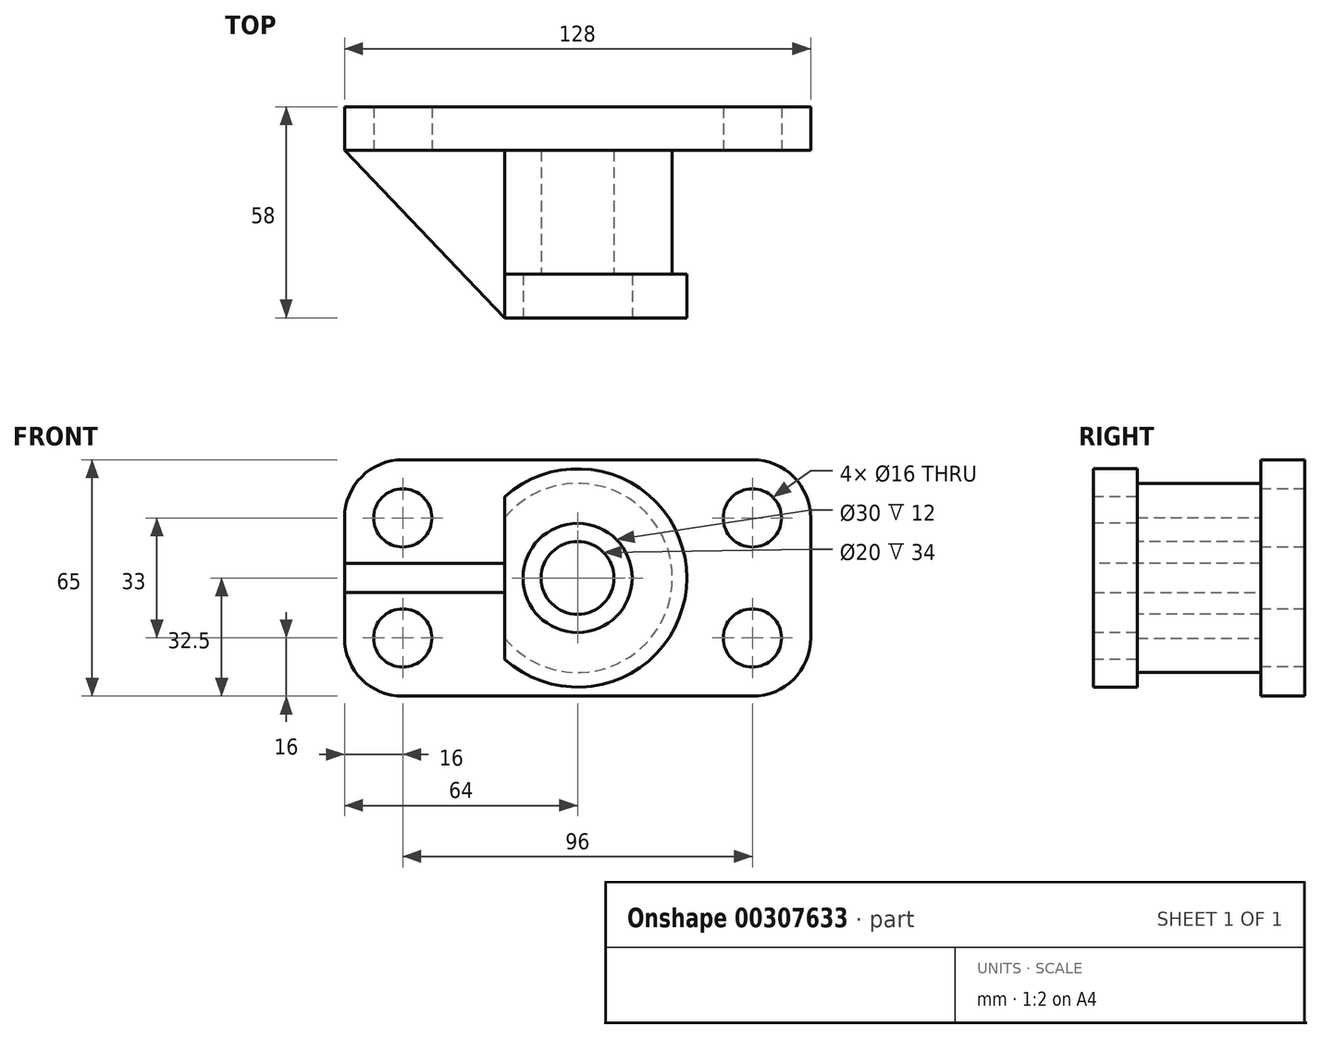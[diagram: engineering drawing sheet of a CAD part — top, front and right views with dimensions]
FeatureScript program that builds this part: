
annotation { "Feature Type Name" : "Feature", "Feature Type Description" : "" }
export const myFeature = defineFeature(function(context is Context, id is Id, definition is map)
    precondition{}
    {
        {
            var Q0;
            Q0=qCreatedBy(makeId("Front.planeOp"),FACE);
            var sketch = newSketch(context, id + "F0", { "sketchPlane" : qUnion([Q0])});
            skLineSegment(sketch, "E0", {"start": v(0, 0) * mm, "end": v(-128, 0) * mm});
            skLineSegment(sketch, "E1", {"start": v(0, 0) * mm, "end": v(0, 65) * mm});
            skLineSegment(sketch, "E2", {"start": v(0, 65) * mm, "end": v(-128, 65) * mm});
            skLineSegment(sketch, "E3", {"start": v(-128, 0) * mm, "end": v(-128, 65) * mm});
            skSolve(sketch);
        }
        {
            var Q0;
            Q0=makeQuery(id+"F0.imprint","IMPRINT",FACE,{"disambiguationData":[TD([[makeQuery(id+"F0.imprint","IMPRINT",EDGE,{"derivedFrom":sQuery(id+"F0.wireOp",EDGE,"E0")}),-1.0]])]});
            extrude(context, id + "F1", {"entities" : qUnion([Q0]), "depth" : 12 * mm});
        }
        {
            var Q0;
            Q0=makeQuery(id+"F1.opExtrude","SWEPT_EDGE",EDGE,{"disambiguationData":[OSD([sQuery(id+"F0.wireOp",EDGE,"E2"),sQuery(id+"F0.wireOp",EDGE,"E3")])]});
            var Q1;
            Q1=makeQuery(id+"F1.opExtrude","SWEPT_EDGE",EDGE,{"disambiguationData":[OSD([sQuery(id+"F0.wireOp",EDGE,"E0"),sQuery(id+"F0.wireOp",EDGE,"E3")])]});
            var Q2;
            Q2=makeQuery(id+"F1.opExtrude","SWEPT_EDGE",EDGE,{"disambiguationData":[OSD([sQuery(id+"F0.wireOp",EDGE,"E1"),sQuery(id+"F0.wireOp",EDGE,"E2")])]});
            var Q3;
            Q3=makeQuery(id+"F1.opExtrude","SWEPT_EDGE",EDGE,{"disambiguationData":[OSD([sQuery(id+"F0.wireOp",EDGE,"E0"),sQuery(id+"F0.wireOp",EDGE,"E1")])]});
            fillet(context, id + "F2", {"entities" : qUnion([Q0, Q1, Q2, Q3]), "radius" : 16 * mm, "tangentPropagation" : true, "allowEdgeOverflow" : false});
        }
        {
            var Q0;
            Q0=makeQuery(id+"F1.opExtrude","CAP_FACE",FACE,{"disambiguationData":[OSD([sQuery(id+"F0.wireOp",EDGE,"E0"),sQuery(id+"F0.wireOp",EDGE,"E1"),sQuery(id+"F0.wireOp",EDGE,"E2"),sQuery(id+"F0.wireOp",EDGE,"E3")])],"isStart":false});
            var sketch = newSketch(context, id + "F3", { "sketchPlane" : qUnion([Q0])});
            skLineSegment(sketch, "E4", {"start": v(-112, 65) * mm, "end": v(-16, 65) * mm});
            skCircle(sketch, "E5", {"center": v(-64, 32.5) * mm, "radius": 26 * mm});
            skSolve(sketch);
        }
        {
            var Q0;
            Q0 = qSketchRegion(id + "F3", true);
            extrude(context, id + "F4", {"entities" : qUnion([Q0]), "operationType" : NewBodyOperationType.ADD, "depth" : 34 * mm});
        }
        {
            var Q0;
            Q0=makeQuery(id+"F4.opExtrude","CAP_FACE",FACE,{"disambiguationData":[OSD([sQuery(id+"F3.wireOp",EDGE,"E5")])],"isStart":false});
            var sketch = newSketch(context, id + "F5", { "sketchPlane" : qUnion([Q0])});
            skCircle(sketch, "E6", {"center": v(-64, 32.5) * mm, "radius": 30 * mm});
            skSolve(sketch);
        }
        {
            var Q0;
            Q0 = qSketchRegion(id + "F5", true);
            extrude(context, id + "F6", {"entities" : qUnion([Q0]), "operationType" : NewBodyOperationType.ADD, "depth" : 12 * mm});
        }
        {
            var Q0;
            Q0=makeQuery(id+"F6.opExtrude","CAP_FACE",FACE,{"disambiguationData":[OSD([sQuery(id+"F5.wireOp",EDGE,"E6")])],"isStart":false});
            var sketch = newSketch(context, id + "F7", { "sketchPlane" : qUnion([Q0])});
            skCircle(sketch, "E7", {"center": v(-64, 32.5) * mm, "radius": 15 * mm});
            skSolve(sketch);
        }
        {
            var Q0;
            Q0 = qSketchRegion(id + "F7", true);
            extrude(context, id + "F8", {"entities" : qUnion([Q0]), "operationType" : NewBodyOperationType.REMOVE, "oppositeDirection" : true, "depth" : 12 * mm});
        }
        {
            var Q0;
            Q0=makeQuery(id+"F8.boolean.opBoolean","COPY",FACE,{"derivedFrom":makeQuery(id+"F8.opExtrude","CAP_FACE",FACE,{"disambiguationData":[OSD([sQuery(id+"F7.wireOp",EDGE,"E7")])],"isStart":false})});
            var sketch = newSketch(context, id + "F9", { "sketchPlane" : qUnion([Q0])});
            skCircle(sketch, "E8", {"center": v(-64, 32.5) * mm, "radius": 10 * mm});
            skSolve(sketch);
        }
        {
            var Q0;
            Q0 = qSketchRegion(id + "F9", true);
            extrude(context, id + "F10", {"entities" : qUnion([Q0]), "operationType" : NewBodyOperationType.REMOVE, "oppositeDirection" : true, "depth" : 34 * mm});
        }
        {
            var Q0;
            Q0=makeQuery(id+"F6.opExtrude","CAP_FACE",FACE,{"disambiguationData":[OSD([sQuery(id+"F5.wireOp",EDGE,"E6")])],"isStart":false});
            var sketch = newSketch(context, id + "F11", { "sketchPlane" : qUnion([Q0])});
            skLineSegment(sketch, "E9", {"start": v(-84, 32.5) * mm, "end": v(-84, 54.86) * mm});
            skLineSegment(sketch, "E10", {"start": v(-84, 32.5) * mm, "end": v(-84, 10.14) * mm});
            skArc(sketch, "E11", {"start": v(-84, 54.86) * mm, "mid": v(-94, 32.5) * mm, "end": v(-84, 10.14) * mm});
            skSolve(sketch);
        }
        {
            var Q0;
            Q0 = qSketchRegion(id + "F11", true);
            extrude(context, id + "F12", {"entities" : qUnion([Q0]), "operationType" : NewBodyOperationType.REMOVE, "oppositeDirection" : true, "depth" : 46 * mm});
        }
        {
            var Q0;
            Q0=makeQuery(id+"F12.boolean.opBoolean","MERGE",FACE,{"derivedFrom":[makeQuery(id+"F1.opExtrude","CAP_FACE",FACE,{"disambiguationData":[OSD([sQuery(id+"F0.wireOp",EDGE,"E0"),sQuery(id+"F0.wireOp",EDGE,"E1"),sQuery(id+"F0.wireOp",EDGE,"E2"),sQuery(id+"F0.wireOp",EDGE,"E3")])],"isStart":false}),makeQuery(id+"F12.opExtrude","CAP_FACE",FACE,{"disambiguationData":[OSD([sQuery(id+"F11.wireOp",EDGE,"E9"),sQuery(id+"F11.wireOp",EDGE,"E10"),sQuery(id+"F11.wireOp",EDGE,"E11")])],"isStart":false})]});
            var sketch = newSketch(context, id + "F13", { "sketchPlane" : qUnion([Q0])});
            skLineSegment(sketch, "E12", {"start": v(-128, 28.5) * mm, "end": v(-128, 36.5) * mm});
            skLineSegment(sketch, "E13", {"start": v(-128, 36.5) * mm, "end": v(-84, 36.5) * mm});
            skLineSegment(sketch, "E14", {"start": v(-128, 28.5) * mm, "end": v(-84, 28.5) * mm});
            skLineSegment(sketch, "E15", {"start": v(-84, 28.5) * mm, "end": v(-84, 36.5) * mm});
            skSolve(sketch);
        }
        {
            var Q0;
            Q0 = qSketchRegion(id + "F13", true);
            extrude(context, id + "F14", {"entities" : qUnion([Q0]), "operationType" : NewBodyOperationType.ADD, "depth" : 46 * mm});
        }
        {
            var Q0;
            Q0=makeQuery(id+"F14.opExtrude","SWEPT_FACE",FACE,{"disambiguationData":[OSD([sQuery(id+"F13.wireOp",EDGE,"E14")])]});
            var sketch = newSketch(context, id + "F15", { "sketchPlane" : qUnion([Q0])});
            skLineSegment(sketch, "E16", {"start": v(-84, 58) * mm, "end": v(-128, 12) * mm});
            skLineSegment(sketch, "E17", {"start": v(-128, 12) * mm, "end": v(-128, 58) * mm});
            skLineSegment(sketch, "E18", {"start": v(-128, 58) * mm, "end": v(-84, 58) * mm});
            skSolve(sketch);
        }
        {
            var Q0;
            Q0 = qSketchRegion(id + "F15", true);
            extrude(context, id + "F16", {"entities" : qUnion([Q0]), "operationType" : NewBodyOperationType.REMOVE, "oppositeDirection" : true, "depth" : 25 * mm});
        }
        {
            var Q0;
            Q0=makeQuery(id+"F12.boolean.opBoolean","MERGE",FACE,{"derivedFrom":[makeQuery(id+"F1.opExtrude","CAP_FACE",FACE,{"disambiguationData":[OSD([sQuery(id+"F0.wireOp",EDGE,"E0"),sQuery(id+"F0.wireOp",EDGE,"E1"),sQuery(id+"F0.wireOp",EDGE,"E2"),sQuery(id+"F0.wireOp",EDGE,"E3")])],"isStart":false}),makeQuery(id+"F12.opExtrude","CAP_FACE",FACE,{"disambiguationData":[OSD([sQuery(id+"F11.wireOp",EDGE,"E9"),sQuery(id+"F11.wireOp",EDGE,"E10"),sQuery(id+"F11.wireOp",EDGE,"E11")])],"isStart":false})]});
            var sketch = newSketch(context, id + "F17", { "sketchPlane" : qUnion([Q0])});
            skCircle(sketch, "E19", {"center": v(-16, 49) * mm, "radius": 8 * mm});
            skCircle(sketch, "E20", {"center": v(-16, 16) * mm, "radius": 8 * mm});
            skCircle(sketch, "E21", {"center": v(-112, 49) * mm, "radius": 8 * mm});
            skCircle(sketch, "E22", {"center": v(-112, 16) * mm, "radius": 8 * mm});
            skSolve(sketch);
        }
        {
            var Q0;
            Q0 = qSketchRegion(id + "F17", true);
            extrude(context, id + "F18", {"entities" : qUnion([Q0]), "operationType" : NewBodyOperationType.REMOVE, "oppositeDirection" : true, "depth" : 25 * mm});
        }
    });
